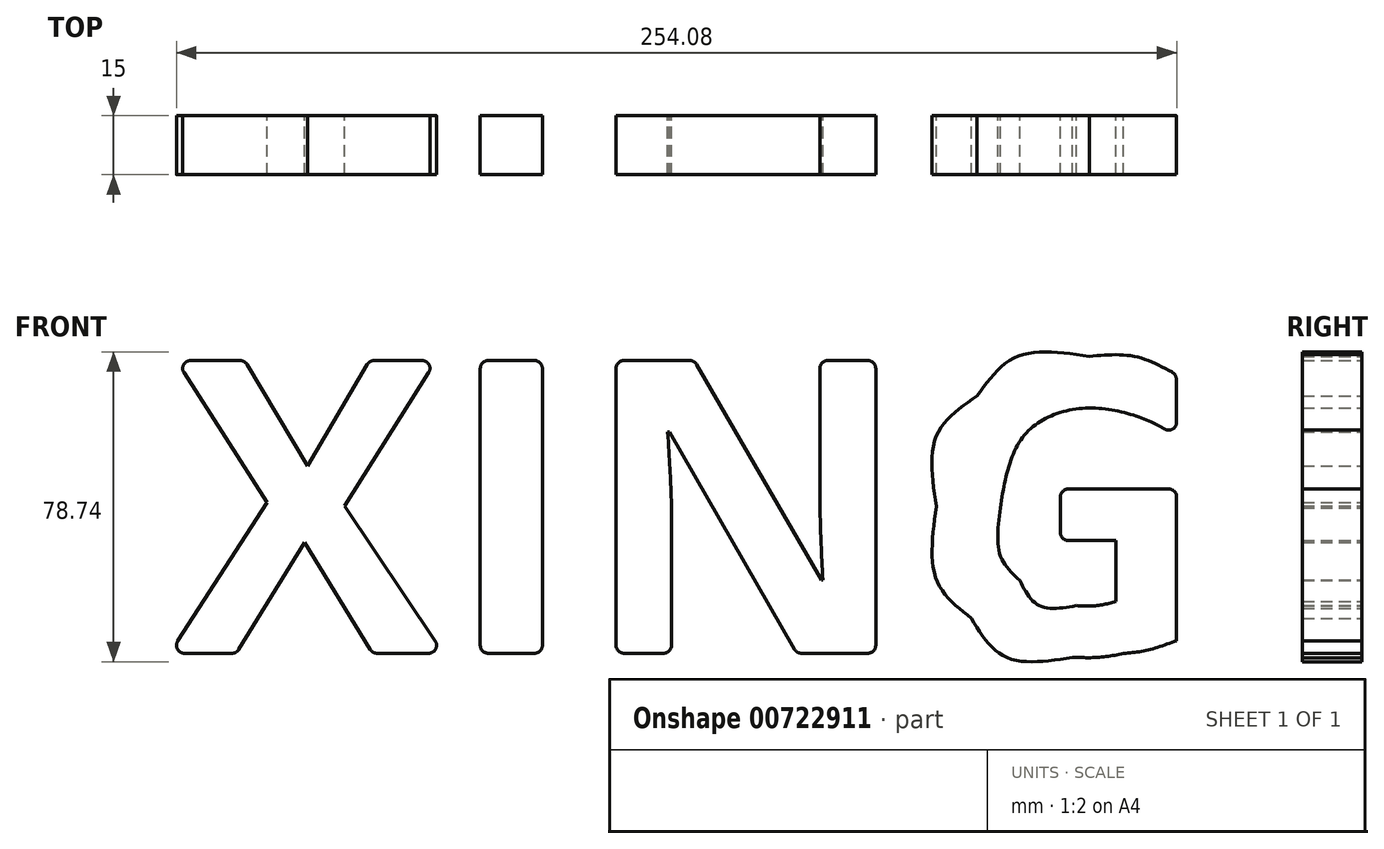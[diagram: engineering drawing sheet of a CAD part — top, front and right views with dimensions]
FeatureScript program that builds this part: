
annotation { "Feature Type Name" : "Feature", "Feature Type Description" : "" }
export const myFeature = defineFeature(function(context is Context, id is Id, definition is map)
    precondition{}
    {
        {
            var Q0;
            Q0=qCreatedBy(makeId("Front.planeOp"),FACE);
            var sketch = newSketch(context, id + "F0", { "sketchPlane" : qUnion([Q0])});
            skText(sketch, "E0", { "text": "XING", "fontName": "OpenSans-Bold.ttf"});
            const initialGuessF0  = {"E0": [-0.13125, 0, 1, 0, 0.075]};
            skSetInitialGuess(sketch, initialGuessF0);
            skSolve(sketch);
        }
        {
            var Q0;
            Q0=makeQuery(id+"F0.imprint","IMPRINT",FACE,{"disambiguationData":[TD([[makeQuery(id+"F0.imprint","IMPRINT",EDGE,{"derivedFrom":sQuery(id+"F0.wireOp",EDGE,"E0.sketch_text.stroke-30")}),-1.0]])]});
            var sketch = newSketch(context, id + "F1", { "sketchPlane" : qUnion([Q0])});
            skLineSegment(sketch, "E1.0.0", {"start": v(94.99, 41.76) * mm, "end": v(94.99, 28.63) * mm});
            skLineSegment(sketch, "E1.0.1", {"start": v(94.99, 28.63) * mm, "end": v(109.08, 28.63) * mm});
            skLineSegment(sketch, "E1.0.2", {"start": v(109.08, 28.63) * mm, "end": v(109.08, 13.12) * mm});
            skFitSpline(sketch, "E1.0.3", {"points": [v(109.08, 13.12) * mm, v(104, 12.1) * mm, v(99.06, 12.1) * mm]});
            skFitSpline(sketch, "E1.0.4", {"points": [v(99.06, 12.1) * mm, v(89.6, 12.1) * mm, v(84.64, 18.49) * mm]});
            skFitSpline(sketch, "E1.0.5", {"points": [v(84.64, 18.49) * mm, v(79.69, 24.87) * mm, v(79.69, 36.98) * mm]});
            skFitSpline(sketch, "E1.0.6", {"points": [v(79.69, 36.98) * mm, v(79.69, 48.57) * mm, v(85.84, 55.44) * mm]});
            skFitSpline(sketch, "E1.0.7", {"points": [v(85.84, 55.44) * mm, v(92, 62.3) * mm, v(102.21, 62.3) * mm]});
            skFitSpline(sketch, "E1.0.8", {"points": [v(102.21, 62.3) * mm, v(111.02, 62.3) * mm, v(119.16, 58.24) * mm]});
            skFitSpline(sketch, "E1.0.10", {"points": [v(124.4, 70.85) * mm, v(113.77, 75.42) * mm, v(102.31, 75.42) * mm]});
            skFitSpline(sketch, "E1.0.11", {"points": [v(102.31, 75.42) * mm, v(84.07, 75.42) * mm, v(73.76, 65.36) * mm]});
            skFitSpline(sketch, "E1.0.12", {"points": [v(73.76, 65.36) * mm, v(63.46, 55.29) * mm, v(63.46, 37.29) * mm]});
            skFitSpline(sketch, "E1.0.13", {"points": [v(63.46, 37.29) * mm, v(63.46, 18.77) * mm, v(72.34, 8.87) * mm]});
            skFitSpline(sketch, "E1.0.14", {"points": [v(72.34, 8.87) * mm, v(81.22, -1.03) * mm, v(98.05, -1.03) * mm]});
            skFitSpline(sketch, "E1.0.15", {"points": [v(98.05, -1.03) * mm, v(104.65, -1.03) * mm, v(110.99, -0.08) * mm]});
            skFitSpline(sketch, "E1.0.16", {"points": [v(110.99, -0.08) * mm, v(117.32, 0.86) * mm, v(124.5, 3.2) * mm]});
            skLineSegment(sketch, "E1.0.17", {"start": v(124.5, 3.2) * mm, "end": v(124.5, 41.76) * mm});
            skLineSegment(sketch, "E1.0.18", {"start": v(124.5, 41.76) * mm, "end": v(94.99, 41.76) * mm});
            skLineSegment(sketch, "E2", {"start": v(124.4, 70.85) * mm, "end": v(124.5, 54.81) * mm});
            skFitSpline(sketch, "E3", {"points": [v(79.69, 36.98) * mm, v(85.84, 55.44) * mm, v(102.21, 62.3) * mm, v(119.16, 58.24) * mm, v(124.5, 54.81) * mm], "startDerivative": vector(11.73, 71.54) * mm, "endDerivative": vector(26.83, -20.39) * mm});
            skSolve(sketch);
        }
        {
            var Q0;
            Q0=makeQuery(id+"F0.imprint","IMPRINT",FACE,{"disambiguationData":[TD([[makeQuery(id+"F0.imprint","IMPRINT",EDGE,{"derivedFrom":sQuery(id+"F0.wireOp",EDGE,"E0.sketch_text.stroke-0")}),-1.0]])]});
            var Q1;
            Q1=makeQuery(id+"F0.imprint","IMPRINT",FACE,{"disambiguationData":[TD([[makeQuery(id+"F0.imprint","IMPRINT",EDGE,{"derivedFrom":sQuery(id+"F0.wireOp",EDGE,"E0.sketch_text.stroke-12")}),-1.0]])]});
            var Q2;
            Q2=makeQuery(id+"F0.imprint","IMPRINT",FACE,{"disambiguationData":[TD([[makeQuery(id+"F0.imprint","IMPRINT",EDGE,{"derivedFrom":sQuery(id+"F0.wireOp",EDGE,"E0.sketch_text.stroke-16")}),-1.0]])]});
            extrude(context, id + "F2", {"entities" : qUnion([Q0, Q1, Q2]), "depth" : 15 * mm, "offsetDistance" : 25 * mm});
        }
        {
            var Q0;
            Q0=makeQuery(id+"F2.opExtrude","SWEPT_EDGE",EDGE,{"disambiguationData":[OSD([sQuery(id+"F0.wireOp",EDGE,"E0.sketch_text.stroke-9"),sQuery(id+"F0.wireOp",EDGE,"E0.sketch_text.stroke-10")])]});
            var Q1;
            Q1=makeQuery(id+"F2.opExtrude","SWEPT_EDGE",EDGE,{"disambiguationData":[OSD([sQuery(id+"F0.wireOp",EDGE,"E0.sketch_text.stroke-8"),sQuery(id+"F0.wireOp",EDGE,"E0.sketch_text.stroke-9")])]});
            var Q2;
            Q2=makeQuery(id+"F2.opExtrude","SWEPT_EDGE",EDGE,{"disambiguationData":[OSD([sQuery(id+"F0.wireOp",EDGE,"E0.sketch_text.stroke-6"),sQuery(id+"F0.wireOp",EDGE,"E0.sketch_text.stroke-7")])]});
            var Q3;
            Q3=makeQuery(id+"F2.opExtrude","SWEPT_EDGE",EDGE,{"disambiguationData":[OSD([sQuery(id+"F0.wireOp",EDGE,"E0.sketch_text.stroke-5"),sQuery(id+"F0.wireOp",EDGE,"E0.sketch_text.stroke-6")])]});
            var Q4;
            Q4=makeQuery(id+"F2.opExtrude","SWEPT_EDGE",EDGE,{"disambiguationData":[OSD([sQuery(id+"F0.wireOp",EDGE,"E0.sketch_text.stroke-3"),sQuery(id+"F0.wireOp",EDGE,"E0.sketch_text.stroke-4")])]});
            var Q5;
            Q5=makeQuery(id+"F2.opExtrude","SWEPT_EDGE",EDGE,{"disambiguationData":[OSD([sQuery(id+"F0.wireOp",EDGE,"E0.sketch_text.stroke-2"),sQuery(id+"F0.wireOp",EDGE,"E0.sketch_text.stroke-3")])]});
            var Q6;
            Q6=makeQuery(id+"F2.opExtrude","SWEPT_EDGE",EDGE,{"disambiguationData":[OSD([sQuery(id+"F0.wireOp",EDGE,"E0.sketch_text.stroke-0"),sQuery(id+"F0.wireOp",EDGE,"E0.sketch_text.stroke-1")])]});
            var Q7;
            Q7=makeQuery(id+"F2.opExtrude","SWEPT_EDGE",EDGE,{"disambiguationData":[OSD([sQuery(id+"F0.wireOp",EDGE,"E0.sketch_text.stroke-0"),sQuery(id+"F0.wireOp",EDGE,"E0.sketch_text.stroke-11")])]});
            var Q8;
            Q8=makeQuery(id+"F2.opExtrude","SWEPT_EDGE",EDGE,{"disambiguationData":[OSD([sQuery(id+"F0.wireOp",EDGE,"E0.sketch_text.stroke-13"),sQuery(id+"F0.wireOp",EDGE,"E0.sketch_text.stroke-14")])]});
            var Q9;
            Q9=makeQuery(id+"F2.opExtrude","SWEPT_EDGE",EDGE,{"disambiguationData":[OSD([sQuery(id+"F0.wireOp",EDGE,"E0.sketch_text.stroke-12"),sQuery(id+"F0.wireOp",EDGE,"E0.sketch_text.stroke-13")])]});
            var Q10;
            Q10=makeQuery(id+"F2.opExtrude","SWEPT_EDGE",EDGE,{"disambiguationData":[OSD([sQuery(id+"F0.wireOp",EDGE,"E0.sketch_text.stroke-12"),sQuery(id+"F0.wireOp",EDGE,"E0.sketch_text.stroke-15")])]});
            var Q11;
            Q11=makeQuery(id+"F2.opExtrude","SWEPT_EDGE",EDGE,{"disambiguationData":[OSD([sQuery(id+"F0.wireOp",EDGE,"E0.sketch_text.stroke-14"),sQuery(id+"F0.wireOp",EDGE,"E0.sketch_text.stroke-15")])]});
            var Q12;
            Q12=makeQuery(id+"F2.opExtrude","SWEPT_EDGE",EDGE,{"disambiguationData":[OSD([sQuery(id+"F0.wireOp",EDGE,"E0.sketch_text.stroke-21"),sQuery(id+"F0.wireOp",EDGE,"E0.sketch_text.stroke-22")])]});
            var Q13;
            Q13=makeQuery(id+"F2.opExtrude","SWEPT_EDGE",EDGE,{"disambiguationData":[OSD([sQuery(id+"F0.wireOp",EDGE,"E0.sketch_text.stroke-20"),sQuery(id+"F0.wireOp",EDGE,"E0.sketch_text.stroke-21")])]});
            var Q14;
            Q14=makeQuery(id+"F2.opExtrude","SWEPT_EDGE",EDGE,{"disambiguationData":[OSD([sQuery(id+"F0.wireOp",EDGE,"E0.sketch_text.stroke-22"),sQuery(id+"F0.wireOp",EDGE,"E0.sketch_text.stroke-23")])]});
            var Q15;
            Q15=makeQuery(id+"F2.opExtrude","SWEPT_EDGE",EDGE,{"disambiguationData":[OSD([sQuery(id+"F0.wireOp",EDGE,"E0.sketch_text.stroke-23"),sQuery(id+"F0.wireOp",EDGE,"E0.sketch_text.stroke-24")])]});
            var Q16;
            Q16=makeQuery(id+"F2.opExtrude","SWEPT_EDGE",EDGE,{"disambiguationData":[OSD([sQuery(id+"F0.wireOp",EDGE,"E0.sketch_text.stroke-27"),sQuery(id+"F0.wireOp",EDGE,"E0.sketch_text.stroke-28")])]});
            var Q17;
            Q17=makeQuery(id+"F2.opExtrude","SWEPT_EDGE",EDGE,{"disambiguationData":[OSD([sQuery(id+"F0.wireOp",EDGE,"E0.sketch_text.stroke-28"),sQuery(id+"F0.wireOp",EDGE,"E0.sketch_text.stroke-29")])]});
            var Q18;
            Q18=makeQuery(id+"F2.opExtrude","SWEPT_EDGE",EDGE,{"disambiguationData":[OSD([sQuery(id+"F0.wireOp",EDGE,"E0.sketch_text.stroke-16"),sQuery(id+"F0.wireOp",EDGE,"E0.sketch_text.stroke-17")])]});
            var Q19;
            Q19=makeQuery(id+"F2.opExtrude","SWEPT_EDGE",EDGE,{"disambiguationData":[OSD([sQuery(id+"F0.wireOp",EDGE,"E0.sketch_text.stroke-16"),sQuery(id+"F0.wireOp",EDGE,"E0.sketch_text.stroke-29")])]});
            var Q20;
            Q20=makeQuery(id+"F2.opExtrude","SWEPT_EDGE",EDGE,{"disambiguationData":[OSD([sQuery(id+"F1.wireOp",EDGE,"E2"),sQuery(id+"F1.wireOp",EDGE,"E3")])]});
            var Q21;
            Q21=makeQuery(id+"F2.opExtrude","SWEPT_EDGE",EDGE,{"disambiguationData":[OSD([sQuery(id+"F0.wireOp",EDGE,"E0.sketch_text.stroke-30"),sQuery(id+"F0.wireOp",EDGE,"E0.sketch_text.stroke-31")])]});
            var Q22;
            Q22=makeQuery(id+"F2.opExtrude","SWEPT_EDGE",EDGE,{"disambiguationData":[OSD([sQuery(id+"F0.wireOp",EDGE,"E0.sketch_text.stroke-30"),sQuery(id+"F0.wireOp",EDGE,"E0.sketch_text.stroke-48")])]});
            var Q23;
            Q23=makeQuery(id+"F2.opExtrude","SWEPT_EDGE",EDGE,{"disambiguationData":[OSD([sQuery(id+"F0.wireOp",EDGE,"E0.sketch_text.stroke-47"),sQuery(id+"F0.wireOp",EDGE,"E0.sketch_text.stroke-48")])]});
            fillet(context, id + "F3", {"entities" : qUnion([Q0, Q1, Q2, Q3, Q4, Q5, Q6, Q7, Q8, Q9, Q10, Q11, Q12, Q13, Q14, Q15, Q16, Q17, Q18, Q19, Q20, Q21, Q22, Q23]), "radius" : 2 * mm, "tangentPropagation" : true, "allowEdgeOverflow" : false});
        }
        {
            var Q0;
            Q0 = qSketchRegion(id + "F1", true);
            extrude(context, id + "F4", {"entities" : qUnion([Q0]), "depth" : 15 * mm, "offsetDistance" : 25 * mm});
        }
        {
            var Q0;
            Q0=makeQuery(id+"F4.opExtrude","SWEPT_EDGE",EDGE,{"disambiguationData":[OSD([sQuery(id+"F0.wireOp",EDGE,"E0.sketch_text.stroke-39"),sQuery(id+"F1.wireOp",EDGE,"E1.0.10"),sQuery(id+"F1.wireOp",EDGE,"E2")])]});
            var Q1;
            Q1=makeQuery(id+"F4.opExtrude","SWEPT_EDGE",EDGE,{"disambiguationData":[OSD([sQuery(id+"F1.wireOp",EDGE,"E2"),sQuery(id+"F1.wireOp",EDGE,"E3")])]});
            var Q2;
            Q2=makeQuery(id+"F4.opExtrude","SWEPT_EDGE",EDGE,{"disambiguationData":[OSD([sQuery(id+"F1.wireOp",EDGE,"E1.0.0"),sQuery(id+"F1.wireOp",EDGE,"E1.0.18")])]});
            var Q3;
            Q3=makeQuery(id+"F4.opExtrude","SWEPT_EDGE",EDGE,{"disambiguationData":[OSD([sQuery(id+"F1.wireOp",EDGE,"E1.0.0"),sQuery(id+"F1.wireOp",EDGE,"E1.0.1")])]});
            var Q4;
            Q4=makeQuery(id+"F4.opExtrude","SWEPT_EDGE",EDGE,{"disambiguationData":[OSD([sQuery(id+"F1.wireOp",EDGE,"E1.0.17"),sQuery(id+"F1.wireOp",EDGE,"E1.0.18")])]});
            fillet(context, id + "F5", {"entities" : qUnion([Q0, Q1, Q2, Q3, Q4]), "radius" : 2 * mm, "tangentPropagation" : true, "allowEdgeOverflow" : false});
        }
    });
